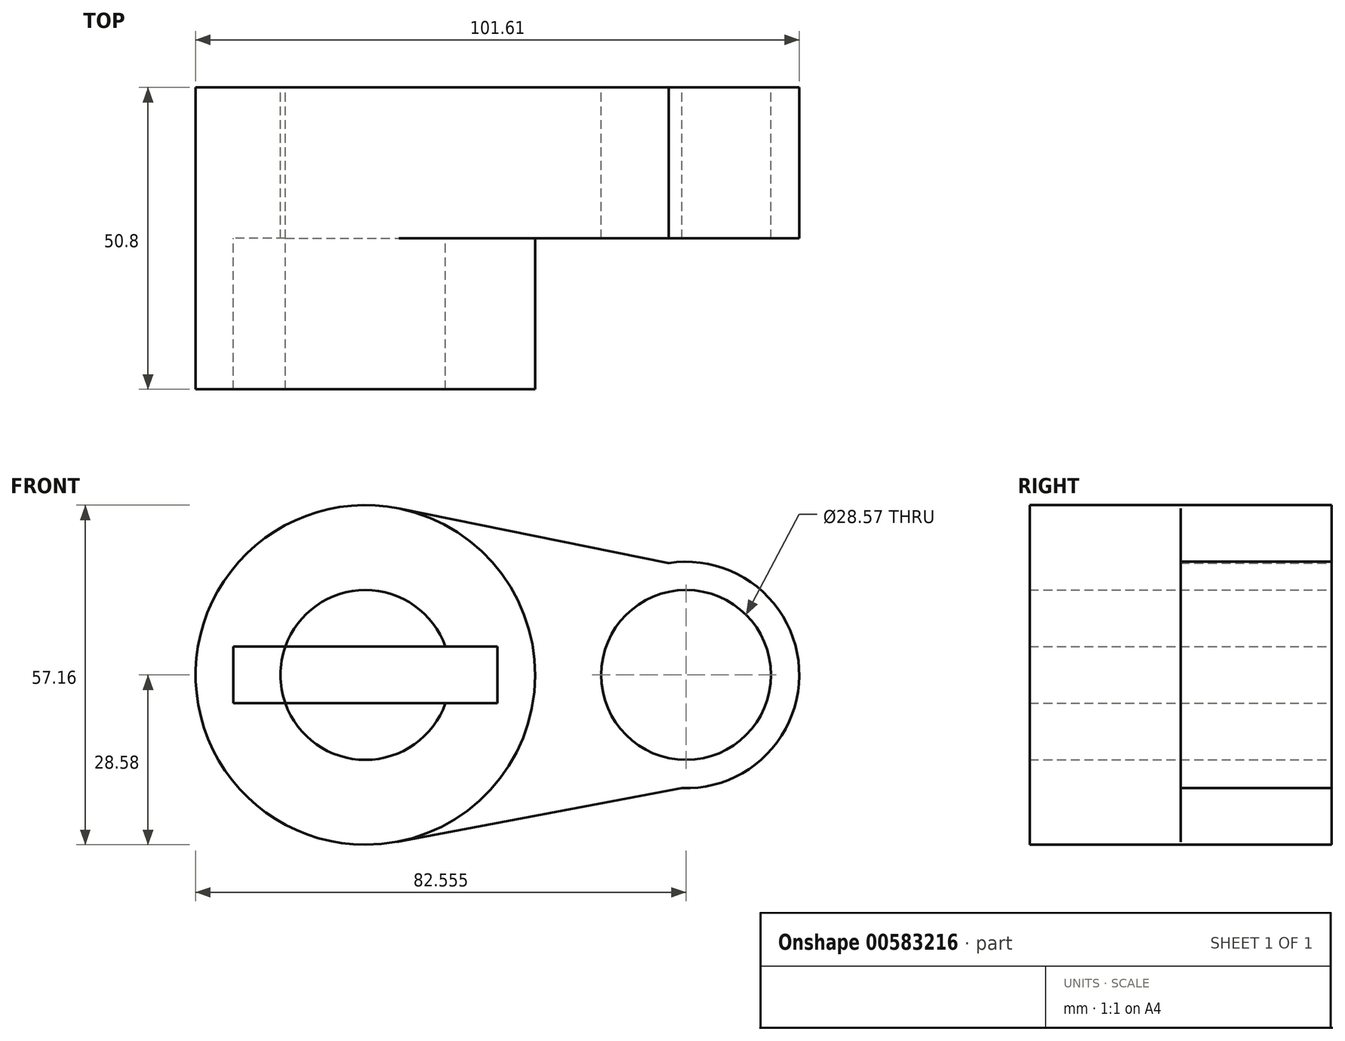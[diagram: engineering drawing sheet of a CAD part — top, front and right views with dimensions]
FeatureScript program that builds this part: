
annotation { "Feature Type Name" : "Feature", "Feature Type Description" : "" }
export const myFeature = defineFeature(function(context is Context, id is Id, definition is map)
    precondition{}
    {
        {
            var Q0;
            Q0=qCreatedBy(makeId("Front.planeOp"),FACE);
            var sketch = newSketch(context, id + "F0", { "sketchPlane" : qUnion([Q0])});
            skCircle(sketch, "E0", {"center": v(0, 0) * mm, "radius": 28.58 * mm});
            skCircle(sketch, "E1", {"center": v(53.98, 0) * mm, "radius": 19.05 * mm});
            skLineSegment(sketch, "E2", {"start": v(5.67, 28) * mm, "end": v(51.06, 18.83) * mm});
            skLineSegment(sketch, "E3", {"start": v(5.29, -28.08) * mm, "end": v(53.3, -19.04) * mm});
            skCircle(sketch, "E4", {"center": v(0, 0) * mm, "radius": 14.29 * mm});
            skCircle(sketch, "E5", {"center": v(53.98, 0) * mm, "radius": 14.29 * mm});
            skLineSegment(sketch, "E6.bottom", {"start": v(-22.23, 4.76) * mm, "end": v(22.23, 4.76) * mm});
            skLineSegment(sketch, "E6.top", {"start": v(-22.23, -4.76) * mm, "end": v(22.22, -4.76) * mm});
            skLineSegment(sketch, "E6.left", {"start": v(-22.23, 4.76) * mm, "end": v(-22.23, -4.76) * mm});
            skLineSegment(sketch, "E6.right", {"start": v(22.23, 4.76) * mm, "end": v(22.22, -4.76) * mm});
            skSolve(sketch);
        }
        {
            var Q0;
            {var subQ7=sQuery(id+"F0.wireOp",EDGE,"E6.left");Q0=makeQuery(id+"F0.imprint","IMPRINT",FACE,{"disambiguationData":[TD([[makeQuery(id+"F0.imprint","IMPRINT",EDGE,{"derivedFrom":subQ7}),-1.0]])]});}
            var Q1;
            Q1=makeQuery(id+"F0.imprint","IMPRINT",FACE,{"disambiguationData":[TD([[makeQuery(id+"F0.imprint","IMPRINT",EDGE,{"derivedFrom":sQuery(id+"F0.wireOp",EDGE,"E5")}),-1.0]])]});
            var Q2;
            {var subQ0=sQuery(id+"F0.wireOp",EDGE,"E2");Q2=makeQuery(id+"F0.imprint","IMPRINT",FACE,{"disambiguationData":[TD([[makeQuery(id+"F0.imprint","IMPRINT",EDGE,{"derivedFrom":subQ0}),-1.0]])]});}
            var Q3;
            {var subQ5=sQuery(id+"F0.wireOp",EDGE,"E6.left");Q3=makeQuery(id+"F0.imprint","IMPRINT",FACE,{"disambiguationData":[TD([[makeQuery(id+"F0.imprint","IMPRINT",EDGE,{"derivedFrom":subQ5}),1.0]])]});}
            extrude(context, id + "F1", {"entities" : qUnion([Q0, Q1, Q2, Q3]), "depth" : 25.4 * mm, "offsetDistance" : 25.4 * mm});
        }
        {
            var Q0;
            {var subQ0=sQuery(id+"F0.wireOp",EDGE,"E6.top");var subQ1=sQuery(id+"F0.wireOp",EDGE,"E4");var subQ2=makeQuery(id+"F0.imprint","INTERSECT",VERTEX,{"disambiguationData":[OD(0.0)],"derivedFrom":[subQ1,subQ0]});Q0=makeQuery(id+"F0.imprint","IMPRINT",FACE,{"disambiguationData":[TD([[makeQuery(id+"F0.imprint","IMPRINT",EDGE,{"disambiguationData":[TD([[subQ2,-1.0]])],"derivedFrom":subQ1}),1.0]])]});}
            var Q1;
            {var subQ0=sQuery(id+"F0.wireOp",EDGE,"E6.bottom");var subQ1=sQuery(id+"F0.wireOp",EDGE,"E4");var subQ2=makeQuery(id+"F0.imprint","INTERSECT",VERTEX,{"disambiguationData":[OD(0.0)],"derivedFrom":[subQ1,subQ0]});Q1=makeQuery(id+"F0.imprint","IMPRINT",FACE,{"disambiguationData":[TD([[makeQuery(id+"F0.imprint","IMPRINT",EDGE,{"disambiguationData":[TD([[subQ2,1.0]])],"derivedFrom":subQ1}),1.0]])]});}
            var Q2;
            {var subQ0=sQuery(id+"F0.wireOp",EDGE,"E2");Q2=makeQuery(id+"F0.imprint","IMPRINT",FACE,{"disambiguationData":[TD([[makeQuery(id+"F0.imprint","IMPRINT",EDGE,{"derivedFrom":subQ0}),-1.0]])]});}
            extrude(context, id + "F2", {"entities" : qUnion([Q0, Q1, Q2]), "operationType" : NewBodyOperationType.ADD, "depth" : 25.4 * mm, "offsetDistance" : 25.4 * mm});
        }
        {
            var Q0;
            {var subQ7=sQuery(id+"F0.wireOp",EDGE,"E6.left");Q0=makeQuery(id+"F0.imprint","IMPRINT",FACE,{"disambiguationData":[TD([[makeQuery(id+"F0.imprint","IMPRINT",EDGE,{"derivedFrom":subQ7}),-1.0]])]});}
            extrude(context, id + "F3", {"entities" : qUnion([Q0]), "operationType" : NewBodyOperationType.ADD, "depth" : 50.8 * mm, "offsetDistance" : 25.4 * mm});
        }
    });
